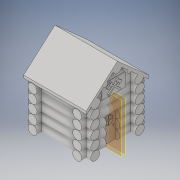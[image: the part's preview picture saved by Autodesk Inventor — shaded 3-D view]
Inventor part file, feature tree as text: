
AUTODESK INVENTOR PART (.ipt)
format: ipt  version: 2018 (Build 220112000, 112)  size: 879,616 bytes
history: native  units: in
note: dims shown in document units (in); Inventor stores cm internally (conversion verified against a paired STEP export)
features: extrude x15, sketch x15, plane x7, mirror x5, chamfer x2, projected_geometry x2, fillet x1
ambient origin geometry x8: Origin, YZ Plane, XZ Plane, XY Plane, X Axis, Y Axis, Z Axis, Center Point
bodies: Solid1 (feature_tree)
feature tree (47):
  extrude  "Extrusion1"  Depth=2.5in
  extrude  "Extrusion2"  Depth=3.5in
  extrude  "Extrusion3"  Depth=0.25in
  sketch  "Sketch4"  dims[d7=0.5in d8=0.5in]
  plane  "Work Plane1"
  mirror  "Mirror1"
  plane  "Work Plane4"
  extrude  "Extrusion4"  Depth=0.5in
  mirror  "Mirror2"
  mirror  "Mirror3"
  plane  "Work Plane7"
  sketch  "Sketch8"  dims[d11=0.25in d12=0.25in]
  extrude  "Extrusion6"  Depth=0.25in
  extrude  "Extrusion7"  Depth=0.25in
  extrude  "Extrusion8"  Depth=0.25in TaperAngle=0.0deg
  mirror  "Mirror4"
  plane  "Work Plane5"
  mirror  "Mirror5"
  plane  "Work Plane6"
  extrude  "Extrusion9"  Depth=0.25in
  extrude  "Extrusion10"  Depth=1.75in
  extrude  "Extrusion11"  Depth=0.25in
  extrude  "Extrusion12"  Depth=0.25in
  extrude  "Extrusion13"  Depth=0.25in
  extrude  "Extrusion14"  Depth=3.5in TaperAngle=0.0deg
  fillet  "Fillet1"  Radius=0.125in
  extrude  "Extrusion15"  TaperAngle=0.0deg  [1 undecoded]
  chamfer  "Chamfer1"  Distance=0.2in
  chamfer  "Chamfer2"  Distance=0.15in
  plane  "Work Plane8"
  extrude  "Extrusion16"  Depth=0.125in
  sketch  "Sketch1"  dims[d0=3.0in d1=2.5in]
  sketch  "Sketch2"  dims[d2=3.5in d3=0.0in d4=0.5in]
  sketch  "Sketch3"  dims[d5=90.0deg d6=0.25in]
  projected_geometry  "Projected Loop1"
  plane  "Work Plane3"
  sketch  "Sketch5"  dims[d9=0.5in d10=0.25in]
  projected_geometry  "Projected Loop2"
  sketch  "Sketch9"  dims[d13=0.25in d14=4.0in d15=0.0in]
  sketch  "Sketch10"  dims[d16=0.25in d17=0.25in]
  sketch  "Sketch11"  dims[d18=0.5in d19=0.0in d20=1.75in]
  sketch  "Sketch12"  dims[d21=0.25in d22=0.25in]
  sketch  "Sketch13"  dims[d23=0.5in d24=0.25in]
  sketch  "Sketch14"  dims[d25=0.25in d26=0.25in]
  sketch  "Sketch15"  dims[d27=0.25in d28=3.5in d29=0.0in d39=0.125in]
  sketch  "Sketch17"  dims[d40=0.125in d42=0.0in]
  sketch  "Sketch19"  dims[d43=0.2in d44=0.2in d45=0.15in d46=0.5in d47=0.136in d48=0.5in d49=0.0in d50=0.34in d51=0.25in d53=1.2in d54=3.5in d55=0.0in d56=3.5in d57=0.0in d58=0.5in d59=0.25in d60=0.5in d61=0.25in d64=0.168in d65=0.168in d66=0.1684in d67=0.25in d68=0.0in d69=1.0in d70=0.0in d71=0.25in d72=-0.225in d73=1.2in d74=1.2in d75=0.85in d76=0.75in d77=1.0in d78=0.0in d79=0.075in d80=0.0375in d81=0.35in d82=0.12in d83=0.15in d84=0.2in d85=0.125in d86=0.3779in d87=0.8921in d88=0.56in d89=0.0in d90=0.0in d91=0.0375in d92=0.575in d93=0.0625in d94=0.0in d96=1.375in d97=1.5in d98=0.75in d99=0.275in d100=0.0in d101=0.5in d102=0.05in d103=0.025in d104=0.375in d105=0.025in d106=0.025in d107=0.4in d108=0.3in d109=0.0in d110=0.08in d111=0.75in d112=0.1in d113=0.1in d114=0.0in d115=0.11in d116=0.07in d117=0.0in d118=0.04in d119=1.0in d120=0.0in d121=0.2in d122=0.125in d123=45.0deg d124=0.1645in d125=0.125in d126=45.0deg d127=0.2in d128=1.0in d129=0.0in]
note: 1 required parameter value undecoded (feature->parameter linkage not recoverable at this tier; creation-order binding heuristic only, values carry confidence <= 0.55)
